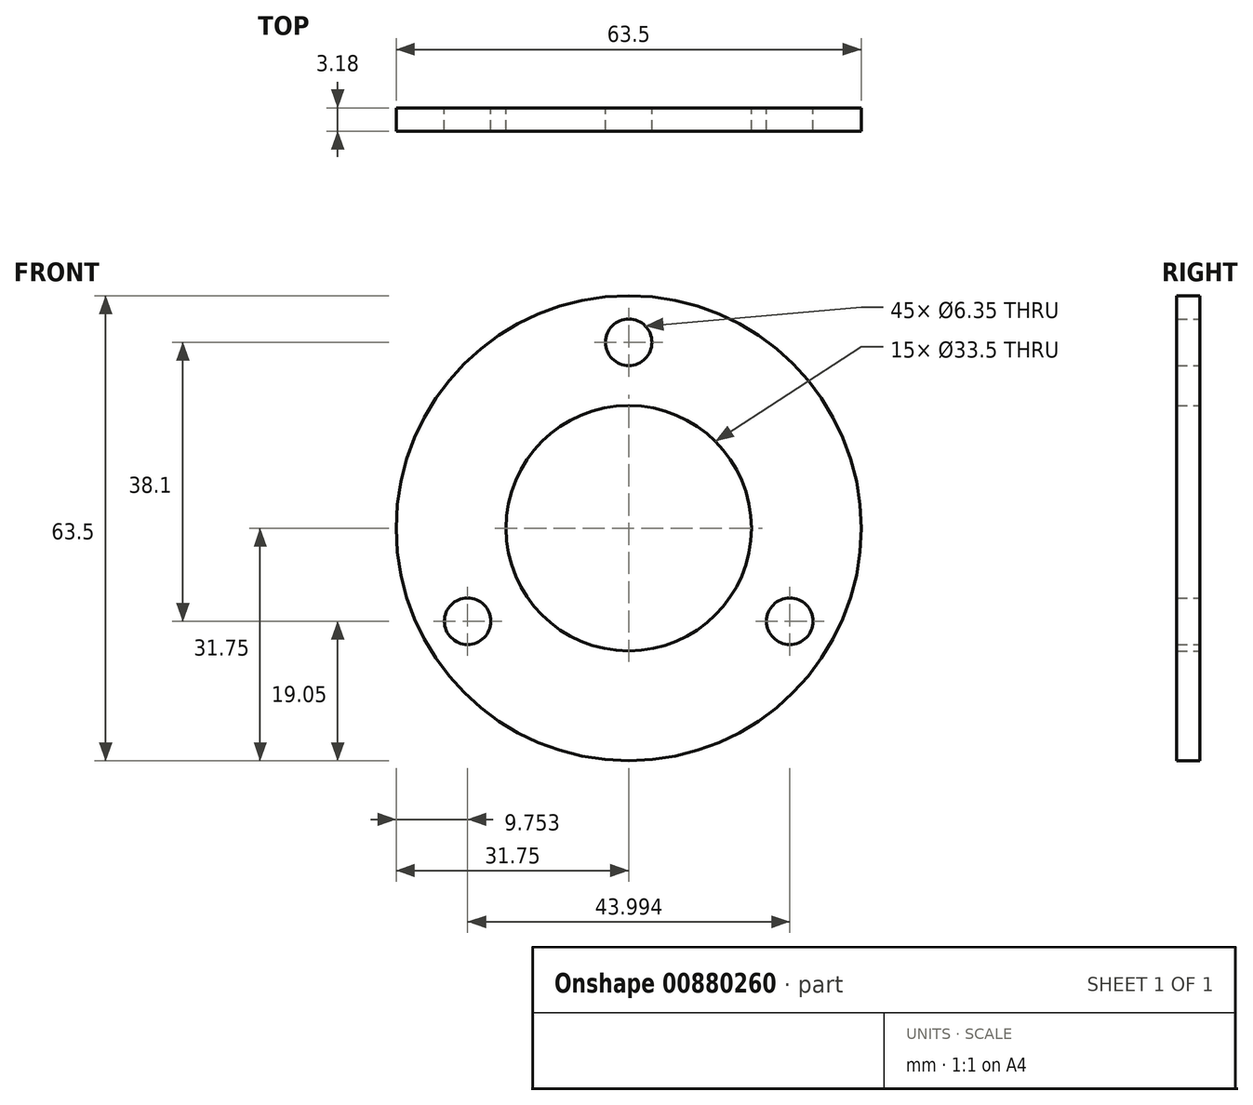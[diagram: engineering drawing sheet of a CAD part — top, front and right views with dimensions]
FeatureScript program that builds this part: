
annotation { "Feature Type Name" : "Feature", "Feature Type Description" : "" }
export const myFeature = defineFeature(function(context is Context, id is Id, definition is map)
    precondition{}
    {
        {
            var Q0;
            Q0=qCreatedBy(makeId("Front.planeOp"),FACE);
            var sketch = newSketch(context, id + "F0", { "sketchPlane" : qUnion([Q0])});
            skCircle(sketch, "E0", {"center": v(0, 0) * mm, "radius": 31.75 * mm});
            skCircle(sketch, "E1", {"center": v(0, 0) * mm, "radius": 16.75 * mm});
            skCircle(sketch, "E2", {"center": v(0, 25.4) * mm, "radius": 3.18 * mm});
            skCircle(sketch, "E3.1.0", {"center": v(-22, -12.7) * mm, "radius": 3.18 * mm});
            skCircle(sketch, "E3.2.0", {"center": v(22, -12.7) * mm, "radius": 3.18 * mm});
            skSolve(sketch);
        }
        {
            var Q0;
            Q0=qSketchRegion(id+"F0",true);
            extrude(context, id + "F1", {"entities" : qUnion([Q0]), "depth" : 3.17 * mm});
        }
    });
